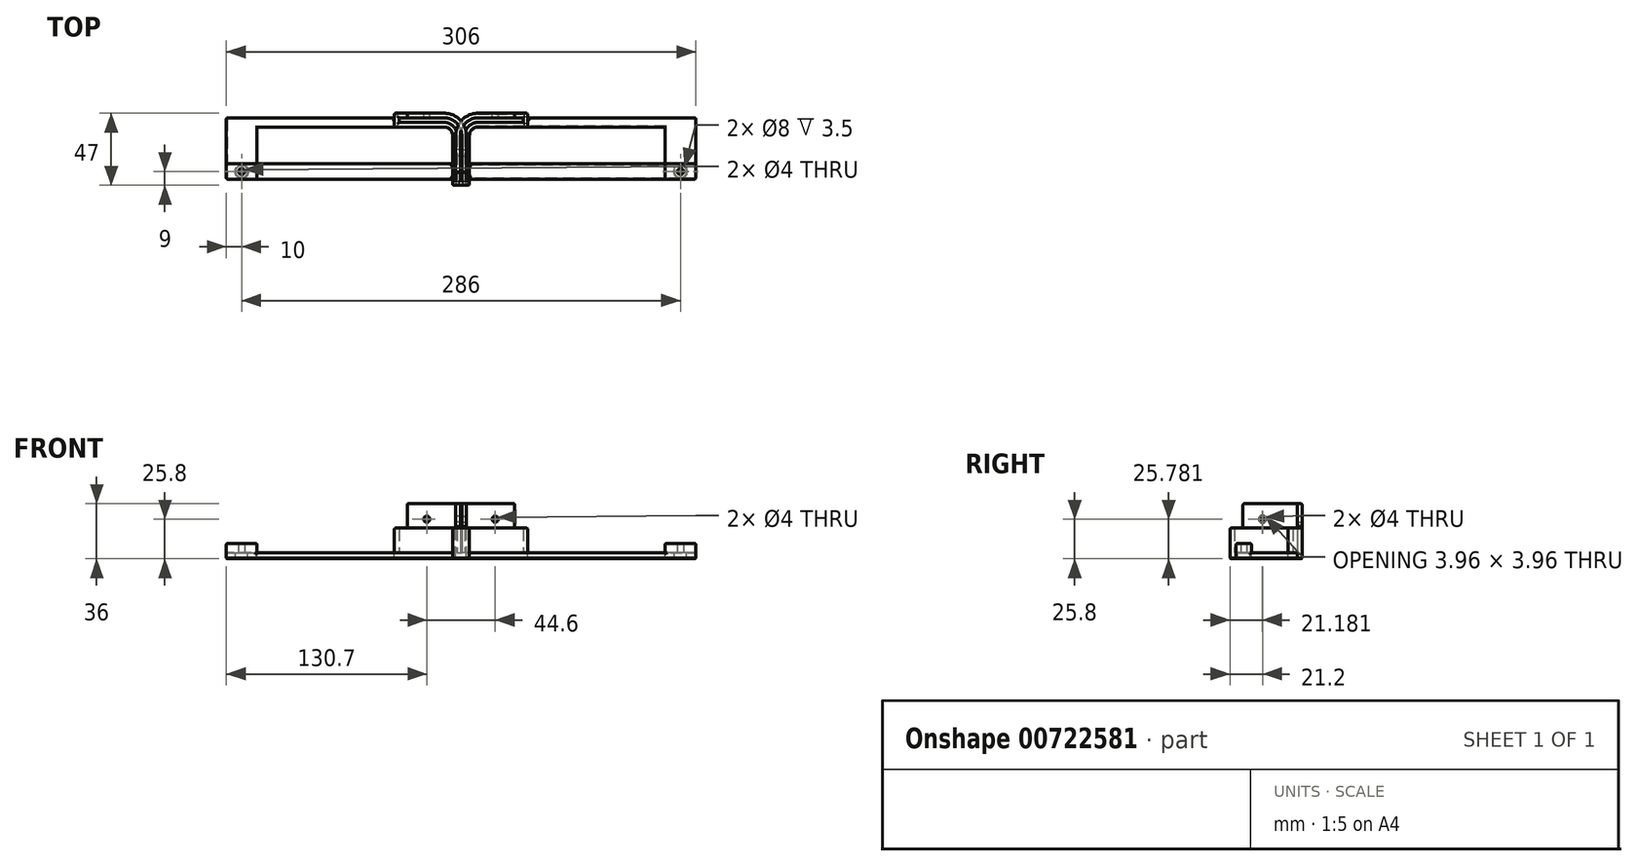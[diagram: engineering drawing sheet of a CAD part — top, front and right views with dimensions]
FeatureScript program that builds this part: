
annotation { "Feature Type Name" : "Feature", "Feature Type Description" : "" }
export const myFeature = defineFeature(function(context is Context, id is Id, definition is map)
    precondition{}
    {
        {
            var Q0;
            Q0=qCreatedBy(makeId("Top.planeOp"),FACE);
            var sketch = newSketch(context, id + "F0", { "sketchPlane" : qUnion([Q0])});
            skLineSegment(sketch, "E0", {"start": v(11, 0) * mm, "end": v(40, 0) * mm, "construction": true});
            skLineSegment(sketch, "E1", {"start": v(0, -11) * mm, "end": v(0, -40) * mm, "construction": true});
            skPoint(sketch, "E2.visualSharp", {"position": v(0, 0) * mm});
            skArc(sketch, "E2.filletArc", {"start": v(11, 0) * mm, "mid": v(3.22, -3.22) * mm, "end": v(0, -11) * mm, "construction": true});
            skLineSegment(sketch, "E3.0", {"start": v(11, -2) * mm, "end": v(40, -2) * mm, "construction": true});
            skArc(sketch, "E3.1", {"start": v(11, -2) * mm, "mid": v(4.64, -4.64) * mm, "end": v(2, -11) * mm, "construction": true});
            skLineSegment(sketch, "E3.2", {"start": v(2, -11) * mm, "end": v(2, -40) * mm, "construction": true});
            skLineSegment(sketch, "E4", {"start": v(40, -2) * mm, "end": v(40, 0) * mm, "construction": true});
            skLineSegment(sketch, "E5", {"start": v(2, -40) * mm, "end": v(0, -40) * mm, "construction": true});
            skArc(sketch, "E6.0", {"start": v(11, 0.5) * mm, "mid": v(2.87, -2.87) * mm, "end": v(-0.5, -11) * mm});
            skLineSegment(sketch, "E6.1", {"start": v(11, 0.5) * mm, "end": v(40.5, 0.5) * mm});
            skLineSegment(sketch, "E6.2", {"start": v(-0.5, -11) * mm, "end": v(-0.5, -40.5) * mm});
            skLineSegment(sketch, "E6.3", {"start": v(40.5, -2.5) * mm, "end": v(40.5, 0.5) * mm});
            skLineSegment(sketch, "E6.4", {"start": v(2.5, -40.5) * mm, "end": v(-0.5, -40.5) * mm});
            skLineSegment(sketch, "E6.5", {"start": v(2.5, -11) * mm, "end": v(2.5, -40.5) * mm});
            skArc(sketch, "E6.6", {"start": v(11, -2.5) * mm, "mid": v(4.99, -4.99) * mm, "end": v(2.5, -11) * mm});
            skLineSegment(sketch, "E6.7", {"start": v(11, -2.5) * mm, "end": v(40.5, -2.5) * mm});
            skLineSegment(sketch, "E7.0", {"start": v(11, 3.5) * mm, "end": v(43.5, 3.5) * mm});
            skLineSegment(sketch, "E7.1", {"start": v(43.5, -5.5) * mm, "end": v(43.5, 3.5) * mm});
            skArc(sketch, "E7.2", {"start": v(11, 3.5) * mm, "mid": v(0.75, -0.75) * mm, "end": v(-3.5, -11) * mm});
            skLineSegment(sketch, "E7.3", {"start": v(11, -5.5) * mm, "end": v(43.5, -5.5) * mm});
            skLineSegment(sketch, "E7.4", {"start": v(-3.5, -11) * mm, "end": v(-3.5, -43.5) * mm});
            skLineSegment(sketch, "E7.5", {"start": v(5.5, -43.5) * mm, "end": v(-3.5, -43.5) * mm});
            skLineSegment(sketch, "E7.6", {"start": v(5.5, -11) * mm, "end": v(5.5, -43.5) * mm});
            skArc(sketch, "E7.7", {"start": v(11, -5.5) * mm, "mid": v(7.11, -7.11) * mm, "end": v(5.5, -11) * mm});
            skLineSegment(sketch, "E8", {"start": v(-3.5, -35) * mm, "end": v(5.5, -35) * mm});
            skLineSegment(sketch, "E9", {"start": v(35, 3.5) * mm, "end": v(35, -5.5) * mm});
            skLineSegment(sketch, "E10", {"start": v(43.5, 0.5) * mm, "end": v(153, 0.5) * mm});
            skLineSegment(sketch, "E11", {"start": v(153, 0.5) * mm, "end": v(153, -39.5) * mm});
            skLineSegment(sketch, "E12", {"start": v(153, -39.5) * mm, "end": v(5.5, -39.5) * mm});
            skLineSegment(sketch, "E13", {"start": v(153, -29.5) * mm, "end": v(5.5, -29.5) * mm});
            skCircle(sketch, "E14", {"center": v(143, -34.5) * mm, "radius": 2 * mm});
            skLineSegment(sketch, "E15", {"start": v(43.5, -5.5) * mm, "end": v(133, -5.5) * mm});
            skLineSegment(sketch, "E16", {"start": v(133, -5.5) * mm, "end": v(133, -29.5) * mm});
            skLineSegment(sketch, "E17", {"start": v(133, -29.5) * mm, "end": v(133, -39.5) * mm});
            skCircle(sketch, "E18", {"center": v(143, -34.5) * mm, "radius": 4 * mm});
            skSolve(sketch);
        }
        {
            var Q0;
            Q0=makeQuery(id+"F0.imprint","IMPRINT",FACE,{"disambiguationData":[TD([[makeQuery(id+"F0.imprint","IMPRINT",EDGE,{"derivedFrom":sQuery(id+"F0.wireOp",EDGE,"E6.0")}),1.0]])]});
            var Q1;
            Q1=makeQuery(id+"F0.imprint","IMPRINT",FACE,{"disambiguationData":[TD([[makeQuery(id+"F0.imprint","IMPRINT",EDGE,{"derivedFrom":sQuery(id+"F0.wireOp",EDGE,"E6.0")}),-1.0]])]});
            var Q2;
            {var subQ0=sQuery(id+"F0.wireOp",EDGE,"E6.3");Q2=makeQuery(id+"F0.imprint","IMPRINT",FACE,{"disambiguationData":[TD([[makeQuery(id+"F0.imprint","IMPRINT",EDGE,{"derivedFrom":subQ0}),1.0]])]});}
            var Q3;
            {var subQ4=sQuery(id+"F0.wireOp",EDGE,"E6.3");Q3=makeQuery(id+"F0.imprint","IMPRINT",FACE,{"disambiguationData":[TD([[makeQuery(id+"F0.imprint","IMPRINT",EDGE,{"derivedFrom":subQ4}),-1.0]])]});}
            var Q4;
            {var subQ5=sQuery(id+"F0.wireOp",EDGE,"E6.6");Q4=makeQuery(id+"F0.imprint","IMPRINT",FACE,{"disambiguationData":[TD([[makeQuery(id+"F0.imprint","IMPRINT",EDGE,{"derivedFrom":subQ5}),1.0]])]});}
            var Q5;
            {var subQ0=sQuery(id+"F0.wireOp",EDGE,"E6.4");Q5=makeQuery(id+"F0.imprint","IMPRINT",FACE,{"disambiguationData":[TD([[makeQuery(id+"F0.imprint","IMPRINT",EDGE,{"derivedFrom":subQ0}),-1.0]])]});}
            var Q6;
            {var subQ1=sQuery(id+"F0.wireOp",EDGE,"E6.4");Q6=makeQuery(id+"F0.imprint","IMPRINT",FACE,{"disambiguationData":[TD([[makeQuery(id+"F0.imprint","IMPRINT",EDGE,{"derivedFrom":subQ1}),1.0]])]});}
            var Q7;
            {var subQ4=sQuery(id+"F0.wireOp",EDGE,"E10");Q7=makeQuery(id+"F0.imprint","IMPRINT",FACE,{"disambiguationData":[TD([[makeQuery(id+"F0.imprint","IMPRINT",EDGE,{"derivedFrom":subQ4}),-1.0]])]});}
            var Q8;
            {var subQ0=sQuery(id+"F0.wireOp",EDGE,"E12");Q8=makeQuery(id+"F0.imprint","IMPRINT",FACE,{"disambiguationData":[TD([[makeQuery(id+"F0.imprint","IMPRINT",EDGE,{"derivedFrom":subQ0}),-1.0]])]});}
            extrude(context, id + "F1", {"entities" : qUnion([Q0, Q1, Q2, Q3, Q4, Q5, Q6, Q7, Q8]), "oppositeDirection" : true, "depth" : 4 * mm, "offsetDistance" : 25 * mm});
        }
        {
            var Q0;
            Q0=makeQuery(id+"F0.imprint","IMPRINT",FACE,{"disambiguationData":[TD([[makeQuery(id+"F0.imprint","IMPRINT",EDGE,{"derivedFrom":sQuery(id+"F0.wireOp",EDGE,"E6.0")}),-1.0]])]});
            var Q1;
            {var subQ1=sQuery(id+"F0.wireOp",EDGE,"E6.4");Q1=makeQuery(id+"F0.imprint","IMPRINT",FACE,{"disambiguationData":[TD([[makeQuery(id+"F0.imprint","IMPRINT",EDGE,{"derivedFrom":subQ1}),1.0]])]});}
            var Q2;
            {var subQ4=sQuery(id+"F0.wireOp",EDGE,"E6.3");Q2=makeQuery(id+"F0.imprint","IMPRINT",FACE,{"disambiguationData":[TD([[makeQuery(id+"F0.imprint","IMPRINT",EDGE,{"derivedFrom":subQ4}),-1.0]])]});}
            var Q3;
            {var subQ5=sQuery(id+"F0.wireOp",EDGE,"E6.6");Q3=makeQuery(id+"F0.imprint","IMPRINT",FACE,{"disambiguationData":[TD([[makeQuery(id+"F0.imprint","IMPRINT",EDGE,{"derivedFrom":subQ5}),1.0]])]});}
            extrude(context, id + "F2", {"entities" : qUnion([Q0, Q1, Q2, Q3]), "operationType" : NewBodyOperationType.ADD, "depth" : 16 * mm, "offsetDistance" : 25 * mm});
        }
        {
            var Q0;
            {var subQ5=sQuery(id+"F0.wireOp",EDGE,"E6.0");Q0=makeQuery(id+"F0.imprint","IMPRINT",FACE,{"disambiguationData":[TD([[makeQuery(id+"F0.imprint","IMPRINT",EDGE,{"derivedFrom":subQ5}),-1.0]])]});}
            extrude(context, id + "F3", {"entities" : qUnion([Q0]), "operationType" : NewBodyOperationType.ADD, "depth" : 32 * mm, "offsetDistance" : 25 * mm});
        }
        {
            var Q0;
            {var subQ0=sQuery(id+"F0.wireOp",EDGE,"E7.4");Q0=makeQuery(id+"F3.boolean.opBoolean","MERGE",FACE,{"derivedFrom":[makeQuery(id+"F2.boolean.opBoolean","MERGE",FACE,{"derivedFrom":[makeQuery(id+"F1.opExtrude","SWEPT_FACE",FACE,{"disambiguationData":[OSD([subQ0])]}),makeQuery(id+"F2.opExtrude","SWEPT_FACE",FACE,{"disambiguationData":[OSD([subQ0])]})]}),makeQuery(id+"F3.opExtrude","SWEPT_FACE",FACE,{"disambiguationData":[OSD([subQ0])]})]});}
            var sketch = newSketch(context, id + "F4", { "sketchPlane" : qUnion([Q0])});
            skCircle(sketch, "E19", {"center": v(22.3, 21.8) * mm, "radius": 2 * mm});
            skSolve(sketch);
        }
        {
            var Q0;
            Q0=makeQuery(id+"F4.imprint","IMPRINT",FACE,{"disambiguationData":[TD([[makeQuery(id+"F4.imprint","IMPRINT",EDGE,{"derivedFrom":sQuery(id+"F4.wireOp",EDGE,"E19")}),1.0]])]});
            extrude(context, id + "F5", {"entities" : qUnion([Q0]), "operationType" : NewBodyOperationType.REMOVE, "oppositeDirection" : true, "depth" : 25 * mm, "offsetDistance" : 25 * mm});
        }
        {
            var Q0;
            {var subQ0=sQuery(id+"F0.wireOp",EDGE,"E7.0");Q0=makeQuery(id+"F3.boolean.opBoolean","MERGE",FACE,{"derivedFrom":[makeQuery(id+"F2.boolean.opBoolean","MERGE",FACE,{"derivedFrom":[makeQuery(id+"F1.opExtrude","SWEPT_FACE",FACE,{"disambiguationData":[OSD([subQ0])]}),makeQuery(id+"F2.opExtrude","SWEPT_FACE",FACE,{"disambiguationData":[OSD([subQ0])]})]}),makeQuery(id+"F3.opExtrude","SWEPT_FACE",FACE,{"disambiguationData":[OSD([subQ0])]})]});}
            var sketch = newSketch(context, id + "F6", { "sketchPlane" : qUnion([Q0])});
            skCircle(sketch, "E20", {"center": v(-22.3, 21.8) * mm, "radius": 2 * mm});
            skSolve(sketch);
        }
        {
            var Q0;
            Q0=makeQuery(id+"F6.imprint","IMPRINT",FACE,{"disambiguationData":[TD([[makeQuery(id+"F6.imprint","IMPRINT",EDGE,{"derivedFrom":sQuery(id+"F6.wireOp",EDGE,"E20")}),1.0]])]});
            extrude(context, id + "F7", {"entities" : qUnion([Q0]), "operationType" : NewBodyOperationType.REMOVE, "oppositeDirection" : true, "depth" : 25 * mm, "offsetDistance" : 25 * mm});
        }
        {
            var Q0;
            Q0=makeQuery(id+"F0.imprint","IMPRINT",FACE,{"disambiguationData":[TD([[makeQuery(id+"F0.imprint","IMPRINT",EDGE,{"derivedFrom":sQuery(id+"F0.wireOp",EDGE,"E14")}),-1.0]])]});
            var Q1;
            {var subQ0=sQuery(id+"F0.wireOp",EDGE,"E17");Q1=makeQuery(id+"F0.imprint","IMPRINT",FACE,{"disambiguationData":[TD([[makeQuery(id+"F0.imprint","IMPRINT",EDGE,{"derivedFrom":subQ0}),1.0]])]});}
            extrude(context, id + "F8", {"entities" : qUnion([Q0, Q1]), "operationType" : NewBodyOperationType.ADD, "depth" : 6 * mm, "offsetDistance" : 25 * mm});
        }
        {
            var Q0;
            Q0=makeQuery(id+"F2.opExtrude","CAP_FACE",FACE,{"disambiguationData":[OSD([sQuery(id+"F0.wireOp",EDGE,"E6.0"),sQuery(id+"F0.wireOp",EDGE,"E6.1"),sQuery(id+"F0.wireOp",EDGE,"E6.2"),sQuery(id+"F0.wireOp",EDGE,"E6.3"),sQuery(id+"F0.wireOp",EDGE,"E6.4"),sQuery(id+"F0.wireOp",EDGE,"E6.5"),sQuery(id+"F0.wireOp",EDGE,"E6.6"),sQuery(id+"F0.wireOp",EDGE,"E6.7"),sQuery(id+"F0.wireOp",EDGE,"E7.0"),sQuery(id+"F0.wireOp",EDGE,"E7.1"),sQuery(id+"F0.wireOp",EDGE,"E7.2"),sQuery(id+"F0.wireOp",EDGE,"E7.3"),sQuery(id+"F0.wireOp",EDGE,"E7.4"),sQuery(id+"F0.wireOp",EDGE,"E7.5"),sQuery(id+"F0.wireOp",EDGE,"E7.6"),sQuery(id+"F0.wireOp",EDGE,"E7.7")])],"isStart":false});
            var Q1;
            Q1=makeQuery(id+"F3.opExtrude","CAP_FACE",FACE,{"disambiguationData":[OSD([sQuery(id+"F0.wireOp",EDGE,"E6.0"),sQuery(id+"F0.wireOp",EDGE,"E6.1"),sQuery(id+"F0.wireOp",EDGE,"E6.2"),sQuery(id+"F0.wireOp",EDGE,"E7.0"),sQuery(id+"F0.wireOp",EDGE,"E7.2"),sQuery(id+"F0.wireOp",EDGE,"E7.4"),sQuery(id+"F0.wireOp",EDGE,"E8"),sQuery(id+"F0.wireOp",EDGE,"E9")])],"isStart":false});
            var Q2;
            {var subQ0=sQuery(id+"F0.wireOp",EDGE,"E7.6");var subQ1=sQuery(id+"F0.wireOp",EDGE,"E7.5");Q2=makeQuery(id+"F2.boolean.opBoolean","MERGE",EDGE,{"derivedFrom":[makeQuery(id+"F1.opExtrude","SWEPT_EDGE",EDGE,{"disambiguationData":[OSD([subQ1,subQ0])]}),makeQuery(id+"F2.opExtrude","SWEPT_EDGE",EDGE,{"disambiguationData":[OSD([subQ1,subQ0])]})]});}
            var Q3;
            {var subQ0=sQuery(id+"F0.wireOp",EDGE,"E7.5");var subQ1=sQuery(id+"F0.wireOp",EDGE,"E7.4");Q3=makeQuery(id+"F2.boolean.opBoolean","MERGE",EDGE,{"derivedFrom":[makeQuery(id+"F1.opExtrude","SWEPT_EDGE",EDGE,{"disambiguationData":[OSD([subQ1,subQ0])]}),makeQuery(id+"F2.opExtrude","SWEPT_EDGE",EDGE,{"disambiguationData":[OSD([subQ1,subQ0])]})]});}
            var Q4;
            {var subQ0=sQuery(id+"F0.wireOp",EDGE,"E7.3");var subQ1=sQuery(id+"F0.wireOp",EDGE,"E7.1");Q4=makeQuery(id+"F2.boolean.opBoolean","MERGE",EDGE,{"derivedFrom":[makeQuery(id+"F1.opExtrude","SWEPT_EDGE",EDGE,{"disambiguationData":[OSD([subQ1,subQ0])]}),makeQuery(id+"F2.opExtrude","SWEPT_EDGE",EDGE,{"disambiguationData":[OSD([subQ1,subQ0])]})]});}
            var Q5;
            {var subQ0=sQuery(id+"F0.wireOp",EDGE,"E7.1");var subQ1=sQuery(id+"F0.wireOp",EDGE,"E7.0");Q5=makeQuery(id+"F2.boolean.opBoolean","MERGE",EDGE,{"derivedFrom":[makeQuery(id+"F1.opExtrude","SWEPT_EDGE",EDGE,{"disambiguationData":[OSD([subQ1,subQ0])]}),makeQuery(id+"F2.opExtrude","SWEPT_EDGE",EDGE,{"disambiguationData":[OSD([subQ1,subQ0])]})]});}
            var Q6;
            Q6=makeQuery(id+"F8.opExtrude","CAP_FACE",FACE,{"disambiguationData":[OSD([sQuery(id+"F0.wireOp",EDGE,"E11"),sQuery(id+"F0.wireOp",EDGE,"E12"),sQuery(id+"F0.wireOp",EDGE,"E13"),sQuery(id+"F0.wireOp",EDGE,"E14"),sQuery(id+"F0.wireOp",EDGE,"E17")])],"isStart":false});
            var Q7;
            Q7=makeQuery(id+"F8.opExtrude","SWEPT_EDGE",EDGE,{"disambiguationData":[OSD([sQuery(id+"F0.wireOp",EDGE,"E13"),sQuery(id+"F0.wireOp",EDGE,"E16"),sQuery(id+"F0.wireOp",EDGE,"E17")])]});
            var Q8;
            {var subQ0=sQuery(id+"F0.wireOp",EDGE,"E12");var subQ1=sQuery(id+"F0.wireOp",EDGE,"E11");Q8=makeQuery(id+"F8.boolean.opBoolean","MERGE",EDGE,{"derivedFrom":[makeQuery(id+"F1.opExtrude","SWEPT_EDGE",EDGE,{"disambiguationData":[OSD([subQ1,subQ0])]}),makeQuery(id+"F8.opExtrude","SWEPT_EDGE",EDGE,{"disambiguationData":[OSD([subQ1,subQ0])]})]});}
            var Q9;
            Q9=makeQuery(id+"F8.opExtrude","SWEPT_EDGE",EDGE,{"disambiguationData":[OSD([sQuery(id+"F0.wireOp",EDGE,"E12"),sQuery(id+"F0.wireOp",EDGE,"E17")])]});
            var Q10;
            Q10=makeQuery(id+"F8.opExtrude","SWEPT_EDGE",EDGE,{"disambiguationData":[OSD([sQuery(id+"F0.wireOp",EDGE,"E11"),sQuery(id+"F0.wireOp",EDGE,"E13")])]});
            var Q11;
            Q11=makeQuery(id+"F1.opExtrude","SWEPT_EDGE",EDGE,{"disambiguationData":[OSD([sQuery(id+"F0.wireOp",EDGE,"E10"),sQuery(id+"F0.wireOp",EDGE,"E11")])]});
            var Q12;
            Q12=makeQuery(id+"F1.opExtrude","SWEPT_EDGE",EDGE,{"disambiguationData":[OSD([sQuery(id+"F0.wireOp",EDGE,"E7.1"),sQuery(id+"F0.wireOp",EDGE,"E10")])]});
            var Q13;
            Q13=makeQuery(id+"F2.opExtrude","SWEPT_EDGE",EDGE,{"disambiguationData":[OSD([sQuery(id+"F0.wireOp",EDGE,"E7.1"),sQuery(id+"F0.wireOp",EDGE,"E7.3"),sQuery(id+"F0.wireOp",EDGE,"E15")])]});
            var Q14;
            Q14=makeQuery(id+"F2.opExtrude","CAP_EDGE",EDGE,{"disambiguationData":[OSD([sQuery(id+"F0.wireOp",EDGE,"E7.1")])],"isStart":true});
            var Q15;
            Q15=makeQuery(id+"F1.opExtrude","CAP_EDGE",EDGE,{"disambiguationData":[OSD([sQuery(id+"F0.wireOp",EDGE,"E10")])],"isStart":true});
            var Q16;
            Q16=makeQuery(id+"F1.opExtrude","CAP_EDGE",EDGE,{"disambiguationData":[OSD([sQuery(id+"F0.wireOp",EDGE,"E11")])],"isStart":true});
            var Q17;
            Q17=makeQuery(id+"F1.opExtrude","CAP_EDGE",EDGE,{"disambiguationData":[OSD([sQuery(id+"F0.wireOp",EDGE,"E12")])],"isStart":true});
            var Q18;
            Q18=makeQuery(id+"F1.opExtrude","SWEPT_EDGE",EDGE,{"disambiguationData":[OSD([sQuery(id+"F0.wireOp",EDGE,"E7.6"),sQuery(id+"F0.wireOp",EDGE,"E12")])]});
            fillet(context, id + "F9", {"entities" : qUnion([Q0, Q1, Q2, Q3, Q4, Q5, Q6, Q7, Q8, Q9, Q10, Q11, Q12, Q13, Q14, Q15, Q16, Q17, Q18]), "radius" : 1 * mm, "tangentPropagation" : true, "allowEdgeOverflow" : false});
        }
        {
            var Q0;
            Q0=makeQuery(id+"F1.opExtrude","CAP_EDGE",EDGE,{"disambiguationData":[OSD([sQuery(id+"F0.wireOp",EDGE,"E13")])],"isStart":true});
            var Q1;
            Q1=makeQuery(id+"F1.opExtrude","CAP_EDGE",EDGE,{"disambiguationData":[OSD([sQuery(id+"F0.wireOp",EDGE,"E16")])],"isStart":true});
            var Q2;
            Q2=makeQuery(id+"F1.opExtrude","SWEPT_EDGE",EDGE,{"disambiguationData":[OSD([sQuery(id+"F0.wireOp",EDGE,"E7.6"),sQuery(id+"F0.wireOp",EDGE,"E13")])]});
            fillet(context, id + "F10", {"entities" : qUnion([Q0, Q1, Q2]), "radius" : 1 * mm, "tangentPropagation" : true, "allowEdgeOverflow" : false});
        }
        {
            var Q0;
            Q0=makeQuery(id+"F1.opExtrude","SWEPT_EDGE",EDGE,{"disambiguationData":[OSD([sQuery(id+"F0.wireOp",EDGE,"E13"),sQuery(id+"F0.wireOp",EDGE,"E16"),sQuery(id+"F0.wireOp",EDGE,"E17")])]});
            var Q1;
            Q1=makeQuery(id+"F8.opExtrude","CAP_EDGE",EDGE,{"disambiguationData":[OSD([sQuery(id+"F0.wireOp",EDGE,"E13")])],"isStart":true});
            var Q2;
            Q2=makeQuery(id+"F8.opExtrude","CAP_EDGE",EDGE,{"disambiguationData":[OSD([sQuery(id+"F0.wireOp",EDGE,"E17")])],"isStart":true});
            fillet(context, id + "F11", {"entities" : qUnion([Q0, Q1, Q2]), "radius" : 1 * mm, "tangentPropagation" : true, "allowEdgeOverflow" : false});
        }
        {
            var Q0;
            Q0=makeQuery(id+"F1.opExtrude","CAP_FACE",FACE,{"disambiguationData":[OSD([sQuery(id+"F0.wireOp",EDGE,"E7.0"),sQuery(id+"F0.wireOp",EDGE,"E7.1"),sQuery(id+"F0.wireOp",EDGE,"E7.2"),sQuery(id+"F0.wireOp",EDGE,"E7.3"),sQuery(id+"F0.wireOp",EDGE,"E7.4"),sQuery(id+"F0.wireOp",EDGE,"E7.5"),sQuery(id+"F0.wireOp",EDGE,"E7.6"),sQuery(id+"F0.wireOp",EDGE,"E7.7"),sQuery(id+"F0.wireOp",EDGE,"E10"),sQuery(id+"F0.wireOp",EDGE,"E11"),sQuery(id+"F0.wireOp",EDGE,"E12"),sQuery(id+"F0.wireOp",EDGE,"E13"),sQuery(id+"F0.wireOp",EDGE,"E15"),sQuery(id+"F0.wireOp",EDGE,"E16"),sQuery(id+"F0.wireOp",EDGE,"E18")])],"isStart":false});
            chamfer(context, id + "F12", {"entities" : qUnion([Q0]), "width" : 0.5 * mm, "tangentPropagation" : true});
        }
        {
            var Q0;
            Q0=makeQuery(id+"F1.opExtrude","SWEPT_BODY",BODY,{"disambiguationData":[OSD([sQuery(id+"F0.wireOp",EDGE,"E7.0"),sQuery(id+"F0.wireOp",EDGE,"E7.1"),sQuery(id+"F0.wireOp",EDGE,"E7.2"),sQuery(id+"F0.wireOp",EDGE,"E7.3"),sQuery(id+"F0.wireOp",EDGE,"E7.4"),sQuery(id+"F0.wireOp",EDGE,"E7.5"),sQuery(id+"F0.wireOp",EDGE,"E7.6"),sQuery(id+"F0.wireOp",EDGE,"E7.7"),sQuery(id+"F0.wireOp",EDGE,"E10"),sQuery(id+"F0.wireOp",EDGE,"E11"),sQuery(id+"F0.wireOp",EDGE,"E12"),sQuery(id+"F0.wireOp",EDGE,"E13"),sQuery(id+"F0.wireOp",EDGE,"E14"),sQuery(id+"F0.wireOp",EDGE,"E15"),sQuery(id+"F0.wireOp",EDGE,"E16")])]});
            var Q1;
            Q1=qCreatedBy(makeId("Right.planeOp"),FACE);
            mirror(context, id + "F13", {"entities" : qUnion([Q0]), "mirrorPlane" : qUnion([Q1])});
        }
    });
